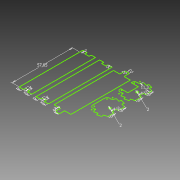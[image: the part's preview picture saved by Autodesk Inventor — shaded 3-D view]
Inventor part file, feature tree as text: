
AUTODESK INVENTOR PART (.ipt)
format: ipt  version: 2012 (Build 160160000, 160)  size: 113,152 bytes
history: native  units: mm
features: sketch x1
ambient origin geometry x8: Origin, YZ Plane, XZ Plane, XY Plane, X Axis, Y Axis, Z Axis, Center Point
feature tree (1):
  sketch  "Sketch1"  dims[d428=4.0mm d429=2.0mm d441=2.0mm d444=6.0mm d445=6.0mm d450=4.0mm d451=2.0mm d452=4.0mm d453=4.0mm d456=2.0mm d457=3.0mm d458=57.85mm d460=4.0mm d461=2.0mm d462=4.0mm d463=4.0mm d467=11.3mm d478=4.0mm d479=2.0mm d480=2.0mm d481=6.0mm d482=6.0mm d487=2.0mm d488=4.0mm d489=2.0mm d490=3.0mm d491=2.0mm]
